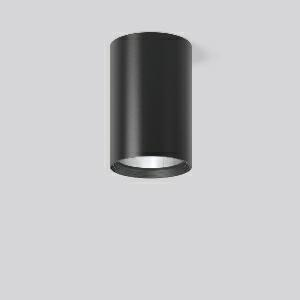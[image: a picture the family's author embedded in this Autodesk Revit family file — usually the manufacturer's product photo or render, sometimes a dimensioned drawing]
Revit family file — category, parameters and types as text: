
# Revit family: heledon_maxi_a_931224_003_2_060c
name_source: partatom
category: Lighting Fixtures
units: mm (PartAtom-declared; Revit-internal decimal feet)

## family parameters
Cut with Voids When Loaded = No
Host = Face
Light Source = No
Part Type = Normal
Room Calculation Point = No
Round Connector Dimension = Use Diameter
Shared = No

## types (1)
- HELEDON maxi A (1 x LED Modul 927, 4100 lm, 2700)
    Apparent Load = 35 VA
    Approval mark = CE
    CIE Flux Codes = 100 100 100 100 100
    Color Rendering = 92
    Color Temperature = 2700
    Default Elevation = 1800 mm
    Description = Series: HELEDON maxi
Cylindrical surface-mounted downlight. Housing: die-cast aluminium, powder-coated. Internal ceiling frame polycarbonate with bayonet mounting. Black plastic ring and recessed LED to prevent glare from the side. Optical assembly with reflector made of MIRO-Silver with 98% total light reflection for outstanding efficiency - can be changed without tools. Best colour rendering index Ra>90. Suitable for Ceiling mounting. Easy installation with a separate ceiling frame with bayonet mounting and plug connection. Driver integrated. Connected via plug-in connector. High quality converter without flickering and stroboscopic effect. The following accessories can be mounted without use of tools: interchangeable lenses, decorative glasses, honeycomb louvre, clear and frosted diffusers, white interchangeable plastic ring. 
Colour: deep black, matt (RAL 9005)
Diameter: 123 mm
Height: 183 mm
Lamp: LED
Socket: without socket
Colour temperature: 2700K
Colour rendering index (CRI): 92
System power: 35 W
Rated luminous flux: 4100 lm
Luminous efficiency: 117 lm/W
Control gear: Regulated power supply
Protection class: I
Type of protection: IP 20
    Height = 183 mm
    Lamp = 1 x LED Modul 927
    Lamp Light Flux = 4100 lm
    Lamp count = 1
    Length = 123 mm
    Lifetime = 50000 h
    Luminous efficacy = 117 lm/W
    Manufacturer = RZB
    ModVariant = No
    Model = 931224.003.2
    Mounting Place = Ceiling
    Mounting Type = Surface mounted
    Number of Poles = 1
    OnlyDefault = Yes
    Power Factor = 1
    Product Name = HELEDON maxi A
    Product group = Surface mounted downlights
    ProductGroupID = 302
    Protection Class = Protection class I
    Protection Degree = IP 20
    RLX_Detail_Level = 1
    RLX_Emergency_Light_Flux = 0 lm
    RLX_Emergency_Type = 0
    RLX_Emergency_Type_DB = No
    RlxData = <blob elided: 96557 chars, md5=6840e522>
    Socket = socket
    Standby Power = 0 W
    System Light Flux = 4100 lm
    System Power = 35 W
    Type Comments = Product without accessories
    Type Image = 931192.003.jpg
    URL = http://relux.com
    VarID = ---
    Voltage = 230 V
    Voltage Range = 220-240 V
    Weight = 0.00 kg
    Width = 0 mm  [stored 0 ft]

note: [stored X ft] marks values corroborated as IEEE doubles in the binary element streams (Revit-internal decimal feet)

## geometry (parser evidence)
native form markers: Blend x4, Sweep x10
no freeform markers — native parametric forms only
